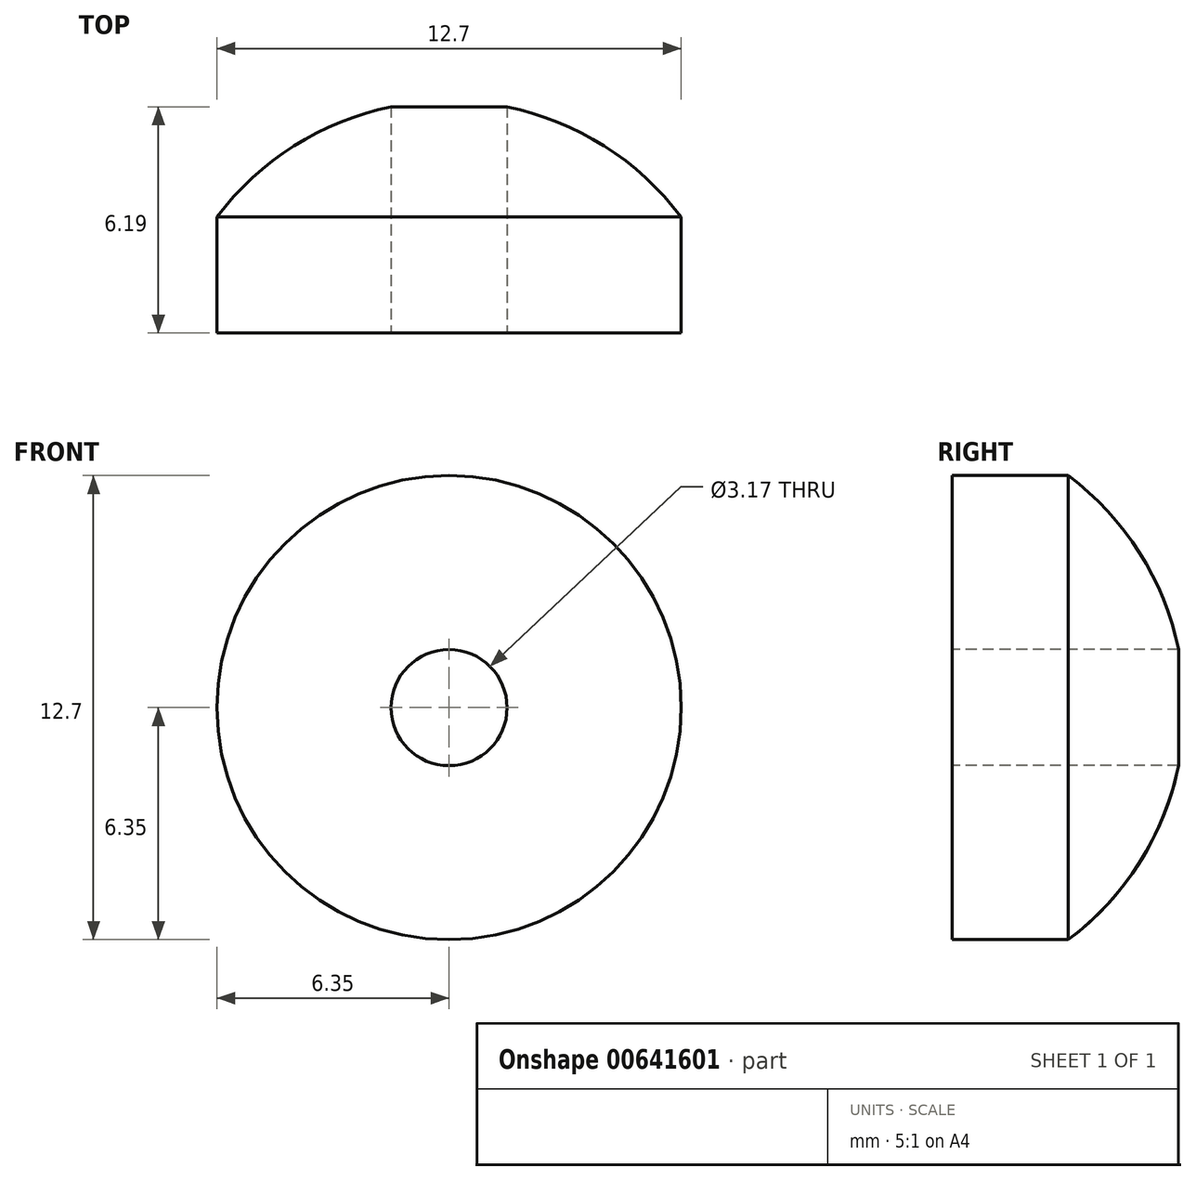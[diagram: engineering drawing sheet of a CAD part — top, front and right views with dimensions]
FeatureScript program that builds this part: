
annotation { "Feature Type Name" : "Feature", "Feature Type Description" : "" }
export const myFeature = defineFeature(function(context is Context, id is Id, definition is map)
    precondition{}
    {
        {
            var Q0;
            Q0=qCreatedBy(makeId("Right.planeOp"),FACE);
            var sketch = newSketch(context, id + "F0", { "sketchPlane" : qUnion([Q0])});
            skLineSegment(sketch, "E0.bottom", {"start": v(0, 0) * mm, "end": v(6.35, 0) * mm});
            skLineSegment(sketch, "E0.top", {"start": v(0, 6.35) * mm, "end": v(6.35, 6.35) * mm});
            skLineSegment(sketch, "E0.left", {"start": v(0, 0) * mm, "end": v(0, 6.35) * mm});
            skLineSegment(sketch, "E0.right", {"start": v(6.35, 0) * mm, "end": v(6.35, 6.35) * mm});
            skArc(sketch, "E1", {"start": v(6.35, 0) * mm, "mid": v(5.51, 3.55) * mm, "end": v(3.17, 6.35) * mm});
            skSolve(sketch);
        }
        {
            var Q0;
            Q0=makeQuery(id+"F0.imprint","IMPRINT",FACE,{"disambiguationData":[TD([[makeQuery(id+"F0.imprint","IMPRINT",EDGE,{"derivedFrom":sQuery(id+"F0.wireOp",EDGE,"E0.bottom")}),1.0]])]});
            var Q1;
            Q1=sQuery(id+"F0.wireOp",EDGE,"E0.bottom");
            revolve(context, id + "F1", {"entities" : qUnion([Q0]), "axis" : qUnion([Q1]), "revolveType" : RevolveType.FULL});
        }
        {
            var Q0;
            Q0=makeQuery(id+"F1.opRevolve","SWEPT_FACE",FACE,{"disambiguationData":[OSD([sQuery(id+"F0.wireOp",EDGE,"E0.left")])]});
            var sketch = newSketch(context, id + "F2", { "sketchPlane" : qUnion([Q0])});
            skPoint(sketch, "E2", {"position": v(0, 0) * mm});
            skSolve(sketch);
        }
        {
            var Q0;
            Q0=sQuery(id+"F2.wireOp",VERTEX,"E2");
            var Q1;
            Q1=makeQuery(id+"F1.opRevolve","SWEPT_BODY",BODY,{"disambiguationData":[OSD([sQuery(id+"F0.wireOp",EDGE,"E0.bottom"),sQuery(id+"F0.wireOp",EDGE,"E0.top"),sQuery(id+"F0.wireOp",EDGE,"E0.left"),sQuery(id+"F0.wireOp",EDGE,"E1")])]});
            hole(context, id + "F3", {"style" : HoleStyle.SIMPLE, "endStyle" : HoleEndStyle.BLIND, "holeDiameter" : 3.17 * mm, "majorDiameter" : 6.35 * mm, "holeDepth" : 12.7 * mm, "isTappedThrough" : true, "tappedDepth" : 12.7 * mm, "tapClearance" : 3, "locations" : qUnion([Q0]), "scope" : qUnion([Q1])});
        }
    });
